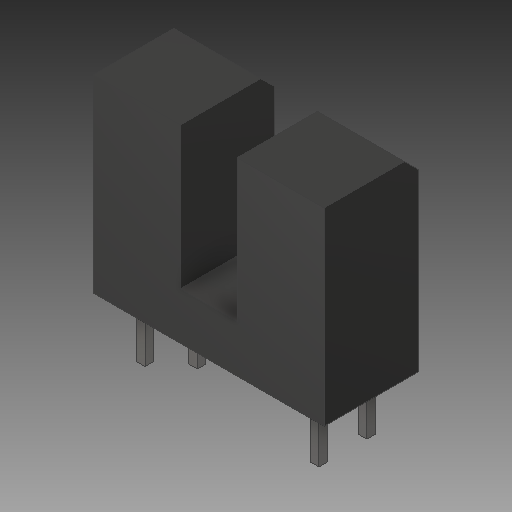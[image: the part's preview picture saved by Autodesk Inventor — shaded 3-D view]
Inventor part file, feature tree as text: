
AUTODESK INVENTOR PART (.ipt)
format: ipt  version: 2018 (Build 220112000, 112)  size: 147,968 bytes
history: native  units: mm
features: sketch x3, extrude x2, chamfer x1
ambient origin geometry x8: Origin, YZ Plane, XZ Plane, XY Plane, X Axis, Y Axis, Z Axis, Center Point
bodies: Solid1 (feature_tree)
feature tree (6):
  extrude  "Extrusion1"  Depth=10.0mm
  sketch  "Sketch2"  dims[d6=1.27mm d7=1.27mm d8=1.5mm d9=9.2mm d10=0.45mm d11=0.45mm d12=3.0mm d13=0.0mm d14=0.75mm d15=2.0mm d16=45.0deg]
  extrude  "Extrusion2"  Depth=3.0mm
  sketch  "Sketch Driven Pattern1"  dims[d0=12.2mm d1=10.0mm]
  chamfer  "Chamfer1"  Distance=5.0mm
  sketch  "Sketch1"  dims[d2=7.5mm d3=3.0mm d4=5.0mm d5=0.0mm]
